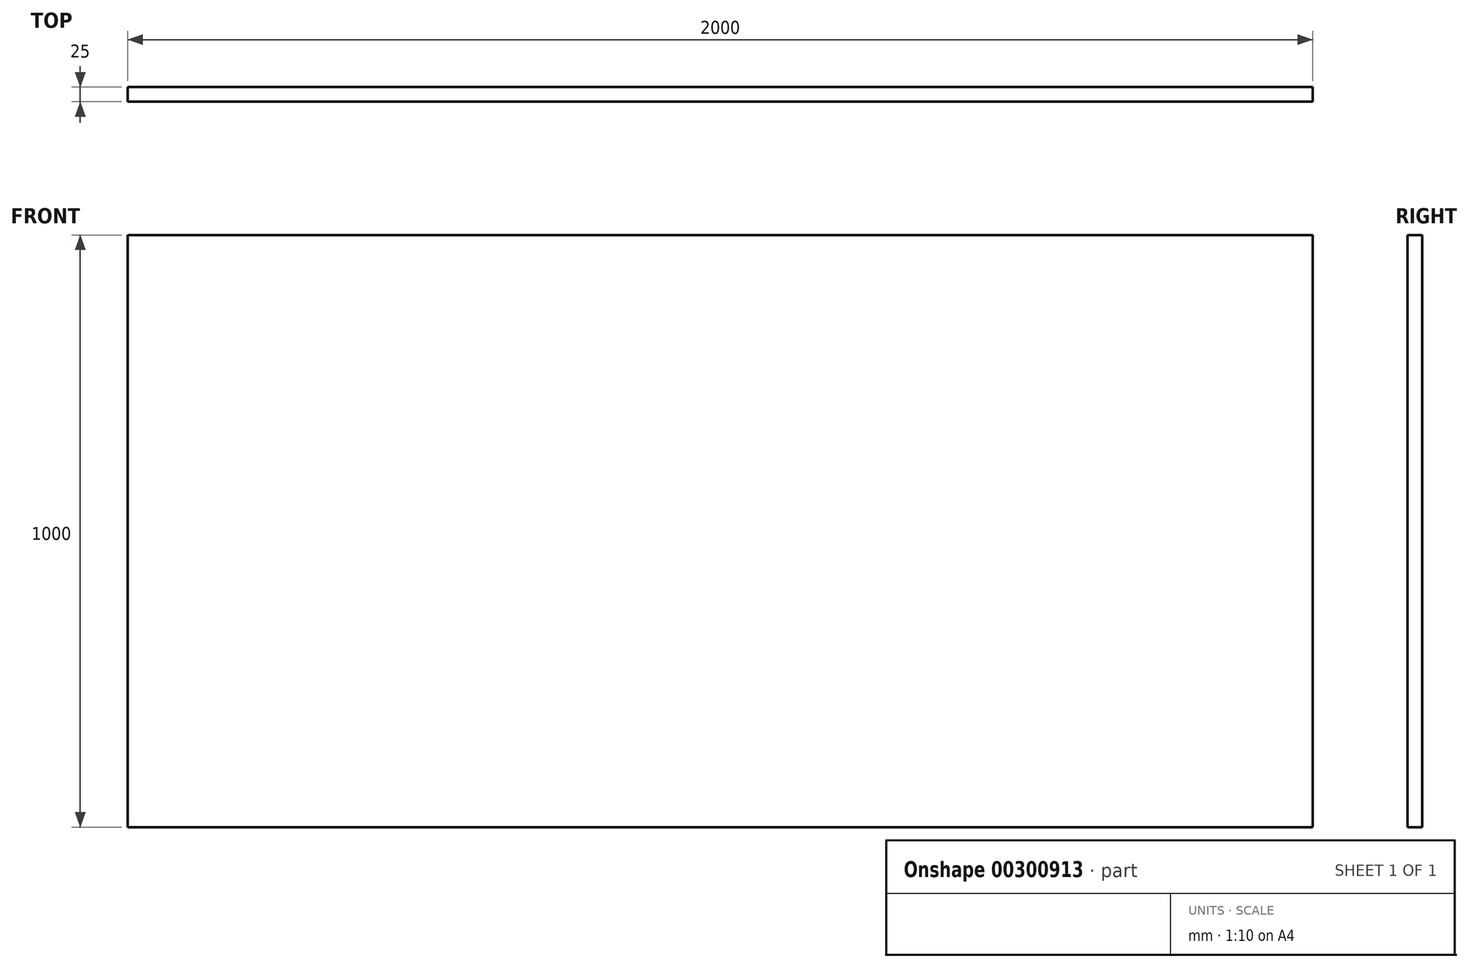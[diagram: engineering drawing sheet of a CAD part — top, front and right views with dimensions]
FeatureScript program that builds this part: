
annotation { "Feature Type Name" : "Feature", "Feature Type Description" : "" }
export const myFeature = defineFeature(function(context is Context, id is Id, definition is map)
    precondition{}
    {
        {
            var Q0;
            Q0=qCreatedBy(makeId("Front.planeOp"),FACE);
            var sketch = newSketch(context, id + "F0", { "sketchPlane" : qUnion([Q0])});
            skLineSegment(sketch, "E0.bottom", {"start": v(0, 0) * mm, "end": v(2000, 0) * mm});
            skLineSegment(sketch, "E0.top", {"start": v(0, 1000) * mm, "end": v(2000, 1000) * mm});
            skLineSegment(sketch, "E0.left", {"start": v(0, 0) * mm, "end": v(0, 1000) * mm});
            skLineSegment(sketch, "E0.right", {"start": v(2000, 0) * mm, "end": v(2000, 1000) * mm});
            skSolve(sketch);
        }
        {
            var Q0;
            Q0=makeQuery(id+"F0.imprint","IMPRINT",FACE,{"disambiguationData":[TD([[makeQuery(id+"F0.imprint","IMPRINT",EDGE,{"derivedFrom":sQuery(id+"F0.wireOp",EDGE,"E0.bottom")}),1.0]])]});
            extrude(context, id + "F1", {"entities" : qUnion([Q0]), "depth" : 25 * mm});
        }
    });
